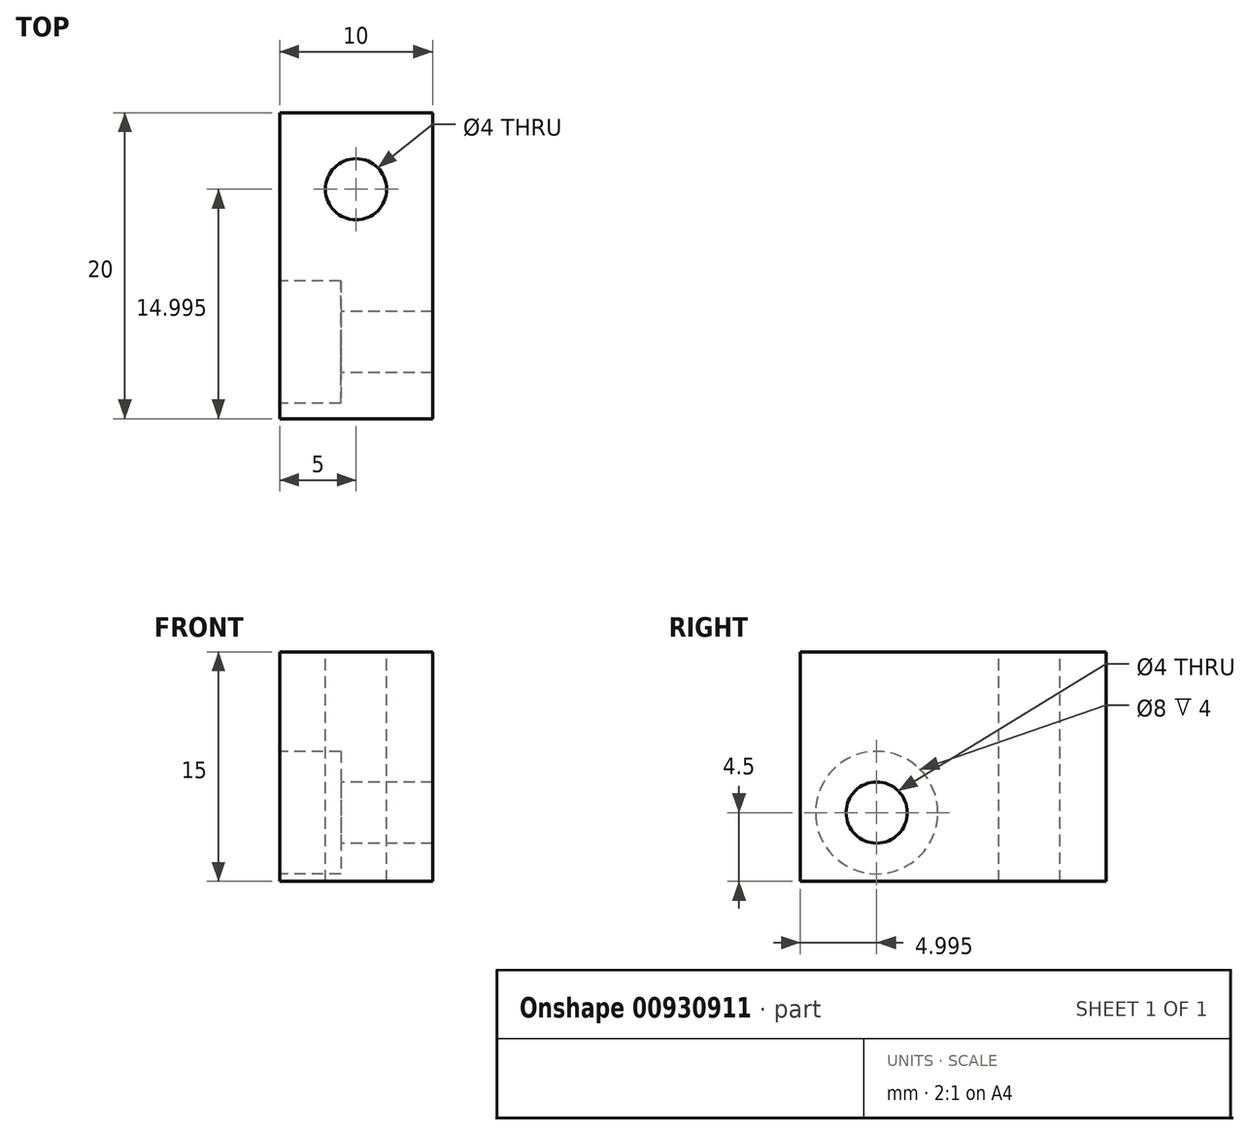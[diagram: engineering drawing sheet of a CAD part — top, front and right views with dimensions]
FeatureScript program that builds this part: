
annotation { "Feature Type Name" : "Feature", "Feature Type Description" : "" }
export const myFeature = defineFeature(function(context is Context, id is Id, definition is map)
    precondition{}
    {
        {
            var Q0;
            Q0=qCreatedBy(makeId("Top.planeOp"),FACE);
            var sketch = newSketch(context, id + "F0", { "sketchPlane" : qUnion([Q0])});
            skLineSegment(sketch, "E0.bottom", {"start": v(-5.85, 14.18) * mm, "end": v(4.15, 14.18) * mm});
            skLineSegment(sketch, "E0.top", {"start": v(-5.85, -5.82) * mm, "end": v(4.15, -5.82) * mm});
            skLineSegment(sketch, "E0.left", {"start": v(-5.85, 14.18) * mm, "end": v(-5.85, -5.82) * mm});
            skLineSegment(sketch, "E0.right", {"start": v(4.15, 14.18) * mm, "end": v(4.15, -5.82) * mm});
            skSolve(sketch);
        }
        {
            var Q0;
            Q0=makeQuery(id+"F0.imprint","IMPRINT",FACE,{"disambiguationData":[TD([[makeQuery(id+"F0.imprint","IMPRINT",EDGE,{"derivedFrom":sQuery(id+"F0.wireOp",EDGE,"E0.bottom")}),-1.0]])]});
            extrude(context, id + "F1", {"entities" : qUnion([Q0]), "depth" : 15 * mm, "offsetDistance" : 25 * mm});
        }
        {
            var Q0;
            Q0=makeQuery(id+"F1.opExtrude","CAP_FACE",FACE,{"disambiguationData":[OSD([sQuery(id+"F0.wireOp",EDGE,"E0.bottom"),sQuery(id+"F0.wireOp",EDGE,"E0.top"),sQuery(id+"F0.wireOp",EDGE,"E0.left"),sQuery(id+"F0.wireOp",EDGE,"E0.right")])],"isStart":false});
            var sketch = newSketch(context, id + "F2", { "sketchPlane" : qUnion([Q0])});
            skCircle(sketch, "E1", {"center": v(-0.85, 9.18) * mm, "radius": 2 * mm});
            skSolve(sketch);
        }
        {
            var Q0;
            Q0=makeQuery(id+"F2.imprint","IMPRINT",FACE,{"disambiguationData":[TD([[makeQuery(id+"F2.imprint","IMPRINT",EDGE,{"derivedFrom":sQuery(id+"F2.wireOp",EDGE,"E1")}),1.0]])]});
            var Q1;
            Q1=sQuery(id+"F2.wireOp",EDGE,"E1");
            extrude(context, id + "F3", {"entities" : qUnion([Q0]), "operationType" : NewBodyOperationType.REMOVE, "surfaceEntities" : qUnion([Q1]), "oppositeDirection" : true, "depth" : 20 * mm, "offsetDistance" : 25 * mm});
        }
        {
            var Q0;
            Q0=makeQuery(id+"F1.opExtrude","SWEPT_FACE",FACE,{"disambiguationData":[OSD([sQuery(id+"F0.wireOp",EDGE,"E0.left")])]});
            var sketch = newSketch(context, id + "F4", { "sketchPlane" : qUnion([Q0])});
            skCircle(sketch, "E2", {"center": v(0.82, 4.5) * mm, "radius": 4 * mm});
            skCircle(sketch, "E3", {"center": v(0.82, 4.5) * mm, "radius": 2 * mm});
            skSolve(sketch);
        }
        {
            var Q0;
            Q0=makeQuery(id+"F4.imprint","IMPRINT",FACE,{"disambiguationData":[TD([[makeQuery(id+"F4.imprint","IMPRINT",EDGE,{"derivedFrom":sQuery(id+"F4.wireOp",EDGE,"E3")}),1.0]])]});
            var Q1;
            Q1=sQuery(id+"F4.wireOp",EDGE,"E3");
            extrude(context, id + "F5", {"entities" : qUnion([Q0]), "operationType" : NewBodyOperationType.REMOVE, "surfaceEntities" : qUnion([Q1]), "oppositeDirection" : true, "depth" : 20 * mm, "offsetDistance" : 25 * mm});
        }
        {
            var Q0;
            Q0=makeQuery(id+"F4.imprint","IMPRINT",FACE,{"disambiguationData":[TD([[makeQuery(id+"F4.imprint","IMPRINT",EDGE,{"derivedFrom":sQuery(id+"F4.wireOp",EDGE,"E2")}),1.0]])]});
            var Q1;
            Q1=sQuery(id+"F4.wireOp",EDGE,"E2");
            extrude(context, id + "F6", {"entities" : qUnion([Q0]), "operationType" : NewBodyOperationType.REMOVE, "surfaceEntities" : qUnion([Q1]), "oppositeDirection" : true, "depth" : 4 * mm, "offsetDistance" : 25 * mm});
        }
    });
